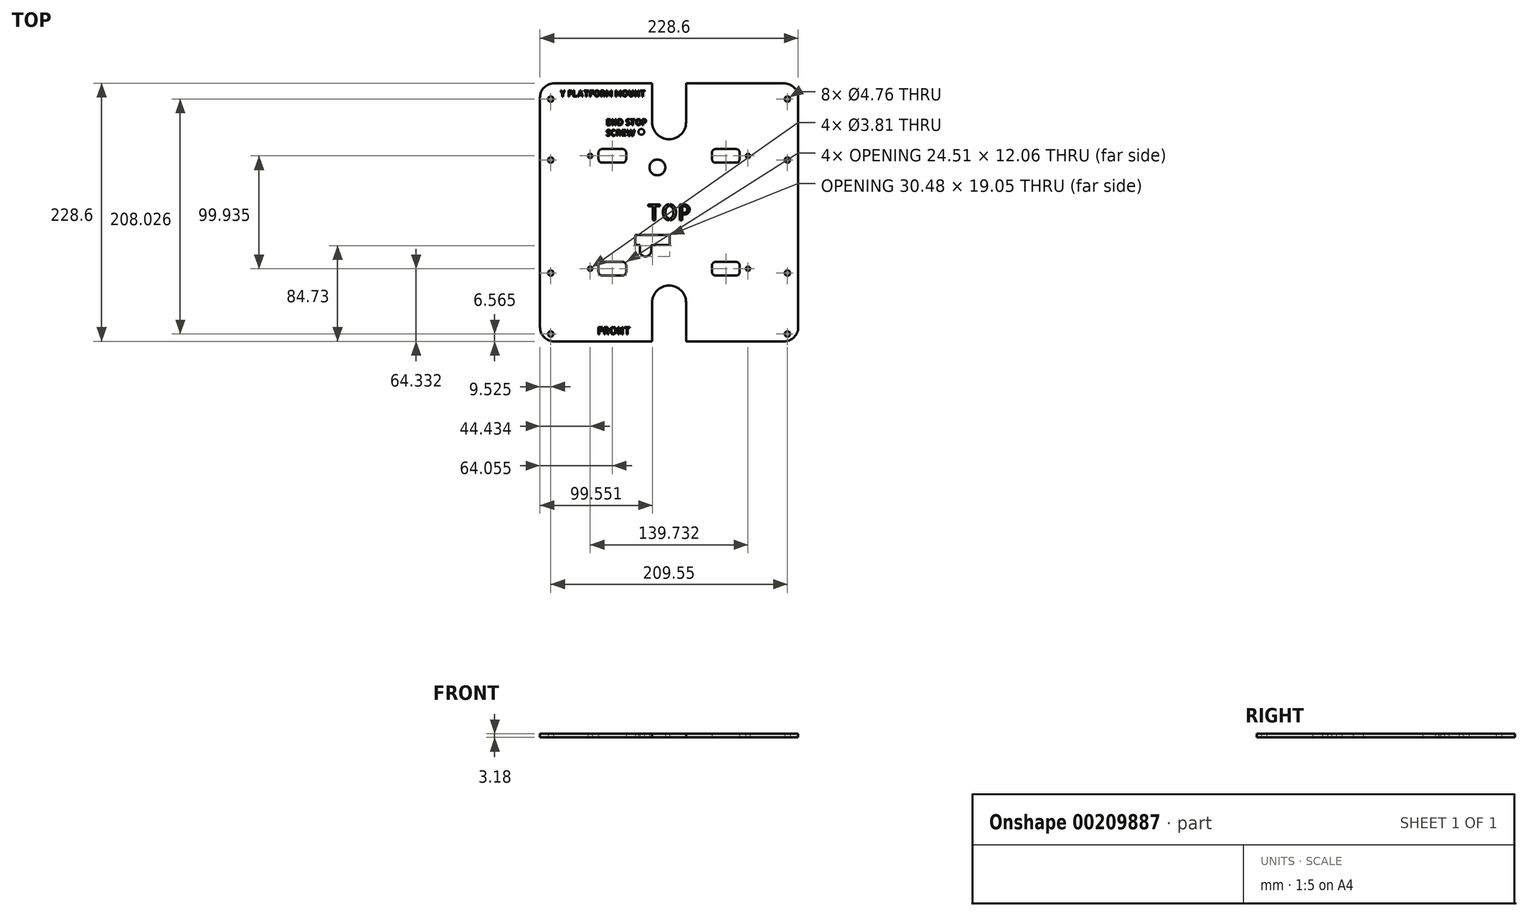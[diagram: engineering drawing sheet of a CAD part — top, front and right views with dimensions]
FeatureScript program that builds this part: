
annotation { "Feature Type Name" : "Feature", "Feature Type Description" : "" }
export const myFeature = defineFeature(function(context is Context, id is Id, definition is map)
    precondition{}
    {
        {
            var Q0;
            Q0=qCreatedBy(makeId("Top.planeOp"),FACE);
            var sketch = newSketch(context, id + "F0", { "sketchPlane" : qUnion([Q0])});
            skLineSegment(sketch, "E0.bottom", {"start": v(-114.3, 114.3) * mm, "end": v(114.3, 114.3) * mm, "construction": true});
            skLineSegment(sketch, "E0.top", {"start": v(-114.3, -114.3) * mm, "end": v(114.3, -114.3) * mm, "construction": true});
            skLineSegment(sketch, "E0.left", {"start": v(-114.3, 101.6) * mm, "end": v(-114.3, -101.6) * mm});
            skLineSegment(sketch, "E0.right", {"start": v(114.3, 101.6) * mm, "end": v(114.3, -101.6) * mm});
            skPoint(sketch, "E1", {"position": v(0, 114.3) * mm});
            skPoint(sketch, "E2", {"position": v(-114.3, 0) * mm});
            skLineSegment(sketch, "E3", {"start": v(-15.05, -114.3) * mm, "end": v(-15.05, -79.82) * mm});
            skLineSegment(sketch, "E4", {"start": v(-15.05, -79.82) * mm, "end": v(15.05, -79.82) * mm, "construction": true});
            skLineSegment(sketch, "E5", {"start": v(15.05, -79.82) * mm, "end": v(15.05, -114.3) * mm});
            skLineSegment(sketch, "E6", {"start": v(-15.05, 114.3) * mm, "end": v(-15.05, 79.82) * mm});
            skLineSegment(sketch, "E7", {"start": v(-15.05, 79.82) * mm, "end": v(15.05, 79.82) * mm, "construction": true});
            skLineSegment(sketch, "E8", {"start": v(15.05, 79.82) * mm, "end": v(15.05, 114.3) * mm});
            skArc(sketch, "E9", {"start": v(-15.05, 79.82) * mm, "mid": v(0, 64.77) * mm, "end": v(15.05, 79.82) * mm});
            skArc(sketch, "E10", {"start": v(15.05, -79.82) * mm, "mid": v(0, -64.77) * mm, "end": v(-15.05, -79.82) * mm});
            skLineSegment(sketch, "E11", {"start": v(-101.6, 114.3) * mm, "end": v(-15.05, 114.3) * mm});
            skLineSegment(sketch, "E12", {"start": v(15.05, 114.3) * mm, "end": v(101.6, 114.3) * mm});
            skLineSegment(sketch, "E13", {"start": v(15.05, -114.3) * mm, "end": v(101.6, -114.3) * mm});
            skLineSegment(sketch, "E14", {"start": v(-15.05, -114.3) * mm, "end": v(-101.6, -114.3) * mm});
            skLineSegment(sketch, "E15.bottom", {"start": v(-59.33, -43.94) * mm, "end": v(-41.16, -43.94) * mm});
            skLineSegment(sketch, "E15.top", {"start": v(-59.33, -56) * mm, "end": v(-41.16, -56) * mm});
            skLineSegment(sketch, "E15.left", {"start": v(-62.5, -47.1) * mm, "end": v(-62.5, -52.83) * mm});
            skLineSegment(sketch, "E15.right", {"start": v(-37.99, -47.1) * mm, "end": v(-37.99, -52.83) * mm});
            skLineSegment(sketch, "E16.bottom", {"start": v(-59.33, 56) * mm, "end": v(-41.16, 56) * mm});
            skLineSegment(sketch, "E16.top", {"start": v(-59.33, 43.94) * mm, "end": v(-41.16, 43.94) * mm});
            skLineSegment(sketch, "E16.left", {"start": v(-62.5, 52.83) * mm, "end": v(-62.5, 47.11) * mm});
            skLineSegment(sketch, "E16.right", {"start": v(-37.99, 52.83) * mm, "end": v(-37.99, 47.11) * mm});
            skLineSegment(sketch, "E17.bottom", {"start": v(41.16, 56) * mm, "end": v(59.33, 56) * mm});
            skLineSegment(sketch, "E17.top", {"start": v(41.16, 43.94) * mm, "end": v(59.33, 43.93) * mm});
            skLineSegment(sketch, "E17.left", {"start": v(37.99, 52.82) * mm, "end": v(37.99, 47.1) * mm});
            skLineSegment(sketch, "E17.right", {"start": v(62.5, 52.82) * mm, "end": v(62.5, 47.1) * mm});
            skLineSegment(sketch, "E18.bottom", {"start": v(41.16, -43.93) * mm, "end": v(59.32, -43.93) * mm});
            skLineSegment(sketch, "E18.top", {"start": v(41.16, -56) * mm, "end": v(59.32, -56) * mm});
            skLineSegment(sketch, "E18.left", {"start": v(37.99, -47.1) * mm, "end": v(37.99, -52.82) * mm});
            skLineSegment(sketch, "E18.right", {"start": v(62.5, -47.1) * mm, "end": v(62.5, -52.82) * mm});
            skPoint(sketch, "E19.visualSharp", {"position": v(-114.3, 114.3) * mm});
            skArc(sketch, "E19.filletArc", {"start": v(-101.6, 114.3) * mm, "mid": v(-110.58, 110.58) * mm, "end": v(-114.3, 101.6) * mm});
            skPoint(sketch, "E20.visualSharp", {"position": v(114.3, 114.3) * mm});
            skArc(sketch, "E20.filletArc", {"start": v(114.3, 101.6) * mm, "mid": v(110.58, 110.58) * mm, "end": v(101.6, 114.3) * mm});
            skPoint(sketch, "E21.visualSharp", {"position": v(114.3, -114.3) * mm});
            skArc(sketch, "E21.filletArc", {"start": v(101.6, -114.3) * mm, "mid": v(110.58, -110.58) * mm, "end": v(114.3, -101.6) * mm});
            skPoint(sketch, "E22.visualSharp", {"position": v(-114.3, -114.3) * mm});
            skArc(sketch, "E22.filletArc", {"start": v(-114.3, -101.6) * mm, "mid": v(-110.58, -110.58) * mm, "end": v(-101.6, -114.3) * mm});
            skPoint(sketch, "E23.visualSharp", {"position": v(-62.5, 56) * mm});
            skArc(sketch, "E23.filletArc", {"start": v(-59.33, 56) * mm, "mid": v(-61.57, 55.07) * mm, "end": v(-62.5, 52.83) * mm});
            skPoint(sketch, "E24.visualSharp", {"position": v(-62.5, 43.94) * mm});
            skArc(sketch, "E24.filletArc", {"start": v(-62.5, 47.11) * mm, "mid": v(-61.57, 44.86) * mm, "end": v(-59.33, 43.94) * mm});
            skPoint(sketch, "E25.visualSharp", {"position": v(-37.99, 56) * mm});
            skArc(sketch, "E25.filletArc", {"start": v(-37.99, 52.83) * mm, "mid": v(-38.92, 55.07) * mm, "end": v(-41.16, 56) * mm});
            skPoint(sketch, "E26.visualSharp", {"position": v(-37.99, 43.94) * mm});
            skArc(sketch, "E26.filletArc", {"start": v(-41.16, 43.94) * mm, "mid": v(-38.92, 44.86) * mm, "end": v(-37.99, 47.11) * mm});
            skPoint(sketch, "E27.visualSharp", {"position": v(37.99, 56) * mm});
            skArc(sketch, "E27.filletArc", {"start": v(41.16, 56) * mm, "mid": v(38.92, 55.07) * mm, "end": v(37.99, 52.82) * mm});
            skPoint(sketch, "E28.visualSharp", {"position": v(37.99, 43.93) * mm});
            skArc(sketch, "E28.filletArc", {"start": v(37.99, 47.1) * mm, "mid": v(38.92, 44.86) * mm, "end": v(41.16, 43.94) * mm});
            skPoint(sketch, "E29.visualSharp", {"position": v(62.5, 56) * mm});
            skArc(sketch, "E29.filletArc", {"start": v(62.5, 52.82) * mm, "mid": v(61.57, 55.07) * mm, "end": v(59.33, 56) * mm});
            skPoint(sketch, "E30.visualSharp", {"position": v(62.5, 43.94) * mm});
            skArc(sketch, "E30.filletArc", {"start": v(59.33, 43.93) * mm, "mid": v(61.57, 44.86) * mm, "end": v(62.5, 47.1) * mm});
            skPoint(sketch, "E31.visualSharp", {"position": v(37.99, -43.93) * mm});
            skArc(sketch, "E31.filletArc", {"start": v(41.16, -43.94) * mm, "mid": v(38.92, -44.86) * mm, "end": v(37.99, -47.1) * mm});
            skPoint(sketch, "E32.visualSharp", {"position": v(37.99, -56) * mm});
            skArc(sketch, "E32.filletArc", {"start": v(37.99, -52.82) * mm, "mid": v(38.92, -55.07) * mm, "end": v(41.16, -56) * mm});
            skPoint(sketch, "E33.visualSharp", {"position": v(62.5, -43.93) * mm});
            skArc(sketch, "E33.filletArc", {"start": v(62.5, -47.1) * mm, "mid": v(61.57, -44.86) * mm, "end": v(59.32, -43.94) * mm});
            skPoint(sketch, "E34.visualSharp", {"position": v(62.5, -56) * mm});
            skArc(sketch, "E34.filletArc", {"start": v(59.32, -56) * mm, "mid": v(61.57, -55.07) * mm, "end": v(62.5, -52.82) * mm});
            skPoint(sketch, "E35.visualSharp", {"position": v(-62.5, -43.94) * mm});
            skArc(sketch, "E35.filletArc", {"start": v(-59.33, -43.94) * mm, "mid": v(-61.57, -44.86) * mm, "end": v(-62.5, -47.1) * mm});
            skPoint(sketch, "E36.visualSharp", {"position": v(-37.99, -43.94) * mm});
            skArc(sketch, "E36.filletArc", {"start": v(-37.99, -47.1) * mm, "mid": v(-38.92, -44.86) * mm, "end": v(-41.16, -43.94) * mm});
            skPoint(sketch, "E37.visualSharp", {"position": v(-37.99, -56) * mm});
            skArc(sketch, "E37.filletArc", {"start": v(-41.16, -56) * mm, "mid": v(-38.92, -55.07) * mm, "end": v(-37.99, -52.83) * mm});
            skPoint(sketch, "E38.visualSharp", {"position": v(-62.5, -56) * mm});
            skArc(sketch, "E38.filletArc", {"start": v(-62.5, -52.83) * mm, "mid": v(-61.57, -55.07) * mm, "end": v(-59.33, -56) * mm});
            skLineSegment(sketch, "E39", {"start": v(-37.99, 49.97) * mm, "end": v(37.99, 49.97) * mm, "construction": true});
            skLineSegment(sketch, "E40", {"start": v(50.24, 43.93) * mm, "end": v(50.24, -43.93) * mm, "construction": true});
            skPoint(sketch, "E41", {"position": v(0, 49.97) * mm});
            skPoint(sketch, "E42", {"position": v(50.24, 0) * mm});
            skCircle(sketch, "E43", {"center": v(-104.78, -53.76) * mm, "radius": 2.38 * mm});
            skLineSegment(sketch, "E44", {"start": v(-104.78, 114.3) * mm, "end": v(-104.77, -114.3) * mm, "construction": true});
            skLineSegment(sketch, "E45", {"start": v(104.78, 114.3) * mm, "end": v(104.77, -114.3) * mm, "construction": true});
            skLineSegment(sketch, "E46", {"start": v(-104.78, 114.3) * mm, "end": v(104.78, 114.3) * mm, "construction": true});
            skCircle(sketch, "E47", {"center": v(104.78, 46.32) * mm, "radius": 2.38 * mm});
            skCircle(sketch, "E48", {"center": v(104.78, -53.76) * mm, "radius": 2.38 * mm});
            skCircle(sketch, "E49", {"center": v(-10.37, 39.79) * mm, "radius": 6.99 * mm});
            skCircle(sketch, "E50", {"center": v(-104.78, 46.32) * mm, "radius": 2.38 * mm});
            skCircle(sketch, "E51", {"center": v(104.78, 100.3) * mm, "radius": 2.38 * mm});
            skCircle(sketch, "E52", {"center": v(-104.78, 100.3) * mm, "radius": 2.38 * mm});
            skCircle(sketch, "E53", {"center": v(104.77, -107.73) * mm, "radius": 2.38 * mm});
            skCircle(sketch, "E54", {"center": v(-104.77, -107.73) * mm, "radius": 2.38 * mm});
            skLineSegment(sketch, "E55", {"start": v(-25.98, -28.93) * mm, "end": v(-29.99, -28.93) * mm});
            skLineSegment(sketch, "E56", {"start": v(-29.99, -28.93) * mm, "end": v(-29.99, -20.04) * mm});
            skLineSegment(sketch, "E57", {"start": v(-29.99, -20.04) * mm, "end": v(0.5, -20.04) * mm});
            skLineSegment(sketch, "E58", {"start": v(0.5, -20.04) * mm, "end": v(0.5, -28.93) * mm});
            skLineSegment(sketch, "E59", {"start": v(0.5, -28.93) * mm, "end": v(-15.82, -28.93) * mm});
            skLineSegment(sketch, "E60", {"start": v(-15.82, -28.93) * mm, "end": v(-15.82, -34.01) * mm});
            skLineSegment(sketch, "E61", {"start": v(-25.98, -28.93) * mm, "end": v(-25.98, -34.01) * mm});
            skArc(sketch, "E62", {"start": v(-25.98, -34.01) * mm, "mid": v(-20.9, -39.1) * mm, "end": v(-15.82, -34.01) * mm});
            skCircle(sketch, "E63", {"center": v(-24.57, 71.24) * mm, "radius": 2.54 * mm});
            skCircle(sketch, "E64", {"center": v(-69.87, 49.97) * mm, "radius": 1.9 * mm});
            skCircle(sketch, "E65", {"center": v(-69.87, -49.97) * mm, "radius": 1.9 * mm});
            skCircle(sketch, "E66", {"center": v(69.87, -49.97) * mm, "radius": 1.9 * mm});
            skCircle(sketch, "E67", {"center": v(69.87, 49.97) * mm, "radius": 1.9 * mm});
            skPoint(sketch, "E68", {"position": v(-62.5, -49.97) * mm});
            skPoint(sketch, "E69", {"position": v(62.5, -49.97) * mm});
            skPoint(sketch, "E70", {"position": v(62.5, 49.97) * mm});
            skPoint(sketch, "E71", {"position": v(-62.5, 49.97) * mm});
            skLineSegment(sketch, "E72", {"start": v(-69.87, 49.97) * mm, "end": v(-62.5, 49.97) * mm, "construction": true});
            skLineSegment(sketch, "E73", {"start": v(-69.87, -49.97) * mm, "end": v(-62.5, -49.97) * mm, "construction": true});
            skLineSegment(sketch, "E74", {"start": v(62.5, -49.97) * mm, "end": v(69.87, -49.97) * mm, "construction": true});
            skLineSegment(sketch, "E75", {"start": v(69.87, 49.97) * mm, "end": v(62.5, 49.97) * mm, "construction": true});
            skPoint(sketch, "E76", {"position": v(-20.9, -39.1) * mm});
            skPoint(sketch, "E77", {"position": v(0, 64.77) * mm});
            skPoint(sketch, "E78", {"position": v(-10.37, 46.77) * mm});
            skSolve(sketch);
        }
        {
            var Q0;
            Q0=makeQuery(id+"F0.imprint","IMPRINT",FACE,{"disambiguationData":[TD([[makeQuery(id+"F0.imprint","IMPRINT",EDGE,{"derivedFrom":sQuery(id+"F0.wireOp",EDGE,"E0.left")}),1.0]])]});
            extrude(context, id + "F1", {"entities" : qUnion([Q0]), "depth" : 3.17 * mm});
        }
        {
            var Q0;
            Q0=makeQuery(id+"F1.opExtrude","CAP_FACE",FACE,{"disambiguationData":[OSD([sQuery(id+"F0.wireOp",EDGE,"E0.left"),sQuery(id+"F0.wireOp",EDGE,"E0.right"),sQuery(id+"F0.wireOp",EDGE,"E3"),sQuery(id+"F0.wireOp",EDGE,"E5"),sQuery(id+"F0.wireOp",EDGE,"E6"),sQuery(id+"F0.wireOp",EDGE,"E8"),sQuery(id+"F0.wireOp",EDGE,"E9"),sQuery(id+"F0.wireOp",EDGE,"E10"),sQuery(id+"F0.wireOp",EDGE,"E11"),sQuery(id+"F0.wireOp",EDGE,"E12"),sQuery(id+"F0.wireOp",EDGE,"E13"),sQuery(id+"F0.wireOp",EDGE,"E14"),sQuery(id+"F0.wireOp",EDGE,"E15.bottom"),sQuery(id+"F0.wireOp",EDGE,"E15.top"),sQuery(id+"F0.wireOp",EDGE,"E15.left"),sQuery(id+"F0.wireOp",EDGE,"E15.right"),sQuery(id+"F0.wireOp",EDGE,"E16.bottom"),sQuery(id+"F0.wireOp",EDGE,"E16.top"),sQuery(id+"F0.wireOp",EDGE,"E16.left"),sQuery(id+"F0.wireOp",EDGE,"E16.right"),sQuery(id+"F0.wireOp",EDGE,"E17.bottom"),sQuery(id+"F0.wireOp",EDGE,"E17.top"),sQuery(id+"F0.wireOp",EDGE,"E17.left"),sQuery(id+"F0.wireOp",EDGE,"E17.right"),sQuery(id+"F0.wireOp",EDGE,"E18.bottom"),sQuery(id+"F0.wireOp",EDGE,"E18.top"),sQuery(id+"F0.wireOp",EDGE,"E18.left"),sQuery(id+"F0.wireOp",EDGE,"E18.right"),sQuery(id+"F0.wireOp",EDGE,"E19.filletArc"),sQuery(id+"F0.wireOp",EDGE,"E20.filletArc"),sQuery(id+"F0.wireOp",EDGE,"E21.filletArc"),sQuery(id+"F0.wireOp",EDGE,"E22.filletArc"),sQuery(id+"F0.wireOp",EDGE,"E23.filletArc"),sQuery(id+"F0.wireOp",EDGE,"E24.filletArc"),sQuery(id+"F0.wireOp",EDGE,"E25.filletArc"),sQuery(id+"F0.wireOp",EDGE,"E26.filletArc"),sQuery(id+"F0.wireOp",EDGE,"E27.filletArc"),sQuery(id+"F0.wireOp",EDGE,"E28.filletArc"),sQuery(id+"F0.wireOp",EDGE,"E29.filletArc"),sQuery(id+"F0.wireOp",EDGE,"E30.filletArc"),sQuery(id+"F0.wireOp",EDGE,"E31.filletArc"),sQuery(id+"F0.wireOp",EDGE,"E32.filletArc"),sQuery(id+"F0.wireOp",EDGE,"E33.filletArc"),sQuery(id+"F0.wireOp",EDGE,"E34.filletArc"),sQuery(id+"F0.wireOp",EDGE,"E35.filletArc"),sQuery(id+"F0.wireOp",EDGE,"E36.filletArc"),sQuery(id+"F0.wireOp",EDGE,"E37.filletArc"),sQuery(id+"F0.wireOp",EDGE,"E38.filletArc"),sQuery(id+"F0.wireOp",EDGE,"E43"),sQuery(id+"F0.wireOp",EDGE,"E47"),sQuery(id+"F0.wireOp",EDGE,"E48"),sQuery(id+"F0.wireOp",EDGE,"E49"),sQuery(id+"F0.wireOp",EDGE,"E50"),sQuery(id+"F0.wireOp",EDGE,"E51"),sQuery(id+"F0.wireOp",EDGE,"E52"),sQuery(id+"F0.wireOp",EDGE,"E53"),sQuery(id+"F0.wireOp",EDGE,"E54"),sQuery(id+"F0.wireOp",EDGE,"E55"),sQuery(id+"F0.wireOp",EDGE,"E56"),sQuery(id+"F0.wireOp",EDGE,"E57"),sQuery(id+"F0.wireOp",EDGE,"E58"),sQuery(id+"F0.wireOp",EDGE,"E59"),sQuery(id+"F0.wireOp",EDGE,"E60"),sQuery(id+"F0.wireOp",EDGE,"E61"),sQuery(id+"F0.wireOp",EDGE,"E62"),sQuery(id+"F0.wireOp",EDGE,"E63"),sQuery(id+"F0.wireOp",EDGE,"E64"),sQuery(id+"F0.wireOp",EDGE,"E65"),sQuery(id+"F0.wireOp",EDGE,"E66"),sQuery(id+"F0.wireOp",EDGE,"E67")])],"isStart":false});
            var sketch = newSketch(context, id + "F2", { "sketchPlane" : qUnion([Q0])});
            skText(sketch, "E79", { "text": "Y PLATFORM MOUNT", "fontName": "AllertaStencil-Regular.ttf"});
            skText(sketch, "E80", { "text": "END STOP\nSCREW", "fontName": "AllertaStencil-Regular.ttf"});
            skLineSegment(sketch, "E81", {"start": v(-114.3, 101.6) * mm, "end": v(-114.3, -101.6) * mm, "construction": true});
            skText(sketch, "E82", { "text": "TOP", "fontName": "AllertaStencil-Regular.ttf"});
            skText(sketch, "E83", { "text": "FRONT", "fontName": "AllertaStencil-Regular.ttf"});
            skPoint(sketch, "E84", {"position": v(19.51, 0) * mm});
            const initialGuessF2  = {"E79": [-0.09652, 0.10262, 1, 0, 0.00533], "E80": [-0.05588, 0.07722, 1, 0, 0.00533], "E82": [-0.01951, -0.00698, 1, 0, 0.01397], "E83": [-0.0635, -0.10795, 1, 0, 0.00635]};
            skSetInitialGuess(sketch, initialGuessF2);
            skSolve(sketch);
        }
        {
            var Q0;
            Q0 = qSketchRegion(id + "F2", true);
            extrude(context, id + "F3", {"entities" : qUnion([Q0]), "operationType" : NewBodyOperationType.REMOVE, "oppositeDirection" : true, "depth" : 0.25 * mm});
        }
    });
